# Revit family: BDG_BossDesign_Stng_Kruze_Lounge-HighBack
name_source: partatom
category: Furniture
revit_build: Autodesk Revit 2015 (Build: 20140903_1530(x64)
units: mm (PartAtom-declared; Revit-internal decimal feet)

## types (3) — shared parameters
Assembly Code = E2020200
AssetType = Movable
BIMObjectName = BDG_BossDesign_Seating_Kruze_Lounge-HighBack
Category = Pr_40_50_12_48 : Lounge chairs
CodePerformance = BS EN 15373:2007
Color = Brown
DurationUnit = year
ExpectedLife = 5
Features = CMHR foam seat and back
IfcExportAs = IfcFurnishingElementType
IfcExportType = CHAIR
Keynote = Pr_40_50_12_48
MainColor = Brown
ManufacturerName = Boss Design
ManufacturerURL = www.bossdesign.com
Material = Leather
NBSDescription = Seating
NBSReference = 45-35-72/352
Name = Seating_Kruze_Lounge-HighBack_BossDesign
NominalHeight = 1100 mm
NominalLength = 770 mm  [stored 2.52625 ft]
NominalWidth = 750 mm  [stored 2.46063 ft]
ProductInformation = www.bossdesign.com/product-list/kruze-lounge/
Shape = Rectangular
Size = 770 x 750 x 1100mm
SustainabilityPerformance = 99% Recyclable
URL = www.bossdesign.com
Uniclass2015Code = Pr_40_50_12_48
Uniclass2015Title = Lounge chairs
Uniclass2015Version = Products v1.9
Version = 1
WarrantyDescription = Structural Warranty Excludes Foams and Fabrics
WarrantyDurationLabor = 5
WarrantyDurationParts = 5
WarrantyDurationUnit = year

## per-type parameters (varying)
| type | Finish | IsUpholsteredShell | IsWoodenShell | Model | ModelNumber | ShellMaterial |
| Fully Upholstered High Back Lounge | Fully upholstered, Chrome frame | Yes | No | KRU/5 | KRU/5 | BDG_Generic_Wood_Walnut_BlackAmerican |
| Oak Outershell High Back Lounge | Oak outershell and Chrome frame | No | Yes | KRU/6/O | KRU/6/O | BDG_Generic_Wood_Oak |
| Walnut Outershell High Back Lounge | Walnut outershell and Chrome frame | No | Yes | KRU/6/W | KRU/6/W | BDG_Generic_Wood_Walnut_BlackAmerican |

note: column(s) folded — value = type name in every type: Description, ModelReference

note: [stored X ft] marks values corroborated as IEEE doubles in the binary element streams (Revit-internal decimal feet)

## geometry (parser evidence)
native form markers: Sweep x3
no freeform markers — native parametric forms only
